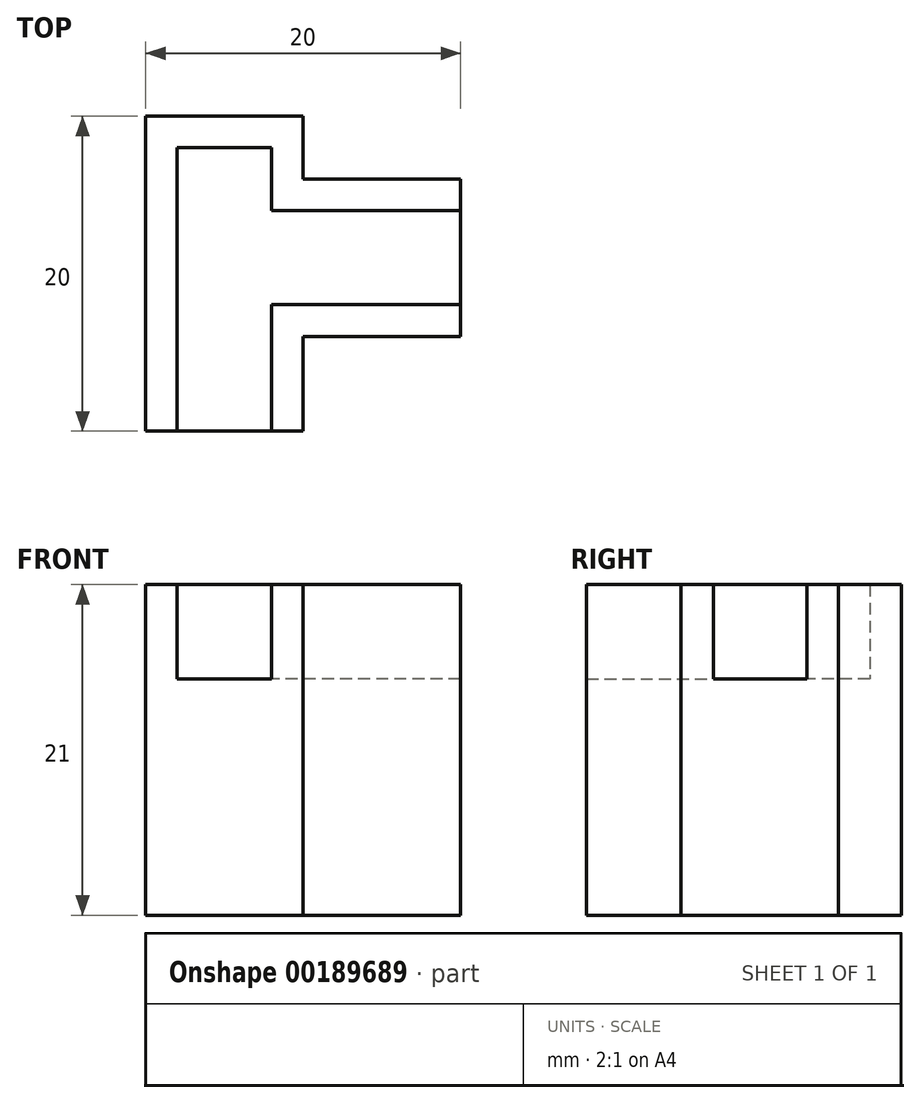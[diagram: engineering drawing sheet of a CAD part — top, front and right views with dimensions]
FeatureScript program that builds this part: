
annotation { "Feature Type Name" : "Feature", "Feature Type Description" : "" }
export const myFeature = defineFeature(function(context is Context, id is Id, definition is map)
    precondition{}
    {
        {
            var Q0;
            Q0=qCreatedBy(makeId("Top.planeOp"),FACE);
            var sketch = newSketch(context, id + "F0", { "sketchPlane" : qUnion([Q0])});
            skLineSegment(sketch, "E0.bottom", {"start": v(-93.24, 33.93) * mm, "end": v(-85.24, 33.93) * mm});
            skLineSegment(sketch, "E0.top", {"start": v(-83.24, 19.93) * mm, "end": v(-73.24, 19.93) * mm});
            skLineSegment(sketch, "E0.left", {"start": v(-93.24, 33.93) * mm, "end": v(-93.24, 19.93) * mm});
            skLineSegment(sketch, "E0.right", {"start": v(-73.24, 29.93) * mm, "end": v(-73.24, 19.93) * mm});
            skLineSegment(sketch, "E1.top", {"start": v(-93.24, 13.93) * mm, "end": v(-83.24, 13.93) * mm});
            skLineSegment(sketch, "E1.left", {"start": v(-93.24, 19.93) * mm, "end": v(-93.24, 13.93) * mm});
            skLineSegment(sketch, "E1.right", {"start": v(-83.24, 19.93) * mm, "end": v(-83.24, 13.93) * mm});
            skLineSegment(sketch, "E2.bottom", {"start": v(-85.24, 33.93) * mm, "end": v(-83.24, 33.93) * mm});
            skLineSegment(sketch, "E3.bottom", {"start": v(-93.24, 33.93) * mm, "end": v(-83.24, 33.93) * mm});
            skLineSegment(sketch, "E3.right", {"start": v(-83.24, 33.93) * mm, "end": v(-83.24, 29.93) * mm});
            skLineSegment(sketch, "E4.top", {"start": v(-73.24, 29.93) * mm, "end": v(-83.24, 29.93) * mm});
            skSolve(sketch);
        }
        {
            var Q0;
            Q0 = qSketchRegion(id + "F0", true);
            extrude(context, id + "F1", {"entities" : qUnion([Q0]), "depth" : 15 * mm});
        }
        {
            var Q0;
            Q0=makeQuery(id+"F1.opExtrude","CAP_FACE",FACE,{"disambiguationData":[OSD([sQuery(id+"F0.wireOp",EDGE,"E0.top"),sQuery(id+"F0.wireOp",EDGE,"E0.right"),sQuery(id+"F0.wireOp",EDGE,"E1.top"),sQuery(id+"F0.wireOp",EDGE,"E1.left"),sQuery(id+"F0.wireOp",EDGE,"E1.right"),sQuery(id+"F0.wireOp",EDGE,"E3.bottom"),sQuery(id+"F0.wireOp",EDGE,"E0.left"),sQuery(id+"F0.wireOp",EDGE,"E4.top"),sQuery(id+"F0.wireOp",EDGE,"E3.right")])],"isStart":false});
            var sketch = newSketch(context, id + "F2", { "sketchPlane" : qUnion([Q0])});
            skLineSegment(sketch, "E5.bottom", {"start": v(-93.24, 33.93) * mm, "end": v(-91.24, 33.93) * mm});
            skLineSegment(sketch, "E5.top", {"start": v(-93.24, 13.93) * mm, "end": v(-91.24, 13.93) * mm});
            skLineSegment(sketch, "E5.left", {"start": v(-93.24, 33.93) * mm, "end": v(-93.24, 13.93) * mm});
            skLineSegment(sketch, "E5.right", {"start": v(-91.24, 31.93) * mm, "end": v(-91.24, 13.93) * mm});
            skLineSegment(sketch, "E6.bottom", {"start": v(-83.24, 33.93) * mm, "end": v(-85.24, 33.93) * mm});
            skLineSegment(sketch, "E6.top", {"start": v(-83.24, 13.93) * mm, "end": v(-85.24, 13.93) * mm});
            skLineSegment(sketch, "E6.left", {"start": v(-83.24, 33.93) * mm, "end": v(-83.24, 29.93) * mm});
            skLineSegment(sketch, "E6.right", {"start": v(-85.24, 31.93) * mm, "end": v(-85.24, 27.93) * mm});
            skLineSegment(sketch, "E7.bottom", {"start": v(-93.24, 33.93) * mm, "end": v(-83.24, 33.93) * mm});
            skLineSegment(sketch, "E7.top", {"start": v(-91.24, 31.93) * mm, "end": v(-85.24, 31.93) * mm});
            skLineSegment(sketch, "E7.left", {"start": v(-93.24, 33.93) * mm, "end": v(-93.24, 31.93) * mm});
            skLineSegment(sketch, "E7.right", {"start": v(-83.24, 33.93) * mm, "end": v(-83.24, 31.93) * mm});
            skLineSegment(sketch, "E8.bottom", {"start": v(-83.24, 29.93) * mm, "end": v(-73.24, 29.93) * mm});
            skLineSegment(sketch, "E8.top", {"start": v(-85.24, 27.93) * mm, "end": v(-73.24, 27.93) * mm});
            skLineSegment(sketch, "E8.left", {"start": v(-85.24, 29.93) * mm, "end": v(-85.24, 27.93) * mm});
            skLineSegment(sketch, "E8.right", {"start": v(-73.24, 29.93) * mm, "end": v(-73.24, 27.93) * mm});
            skLineSegment(sketch, "E9.bottom", {"start": v(-73.24, 19.93) * mm, "end": v(-83.24, 19.93) * mm});
            skLineSegment(sketch, "E9.top", {"start": v(-73.24, 21.98) * mm, "end": v(-85.24, 21.98) * mm});
            skLineSegment(sketch, "E9.left", {"start": v(-73.24, 19.93) * mm, "end": v(-73.24, 21.98) * mm});
            skLineSegment(sketch, "E9.right", {"start": v(-85.24, 19.93) * mm, "end": v(-85.24, 21.98) * mm});
            skLineSegment(sketch, "E10.trimOffspring", {"start": v(-83.24, 19.93) * mm, "end": v(-83.24, 13.93) * mm});
            skLineSegment(sketch, "E11.trimOffspring", {"start": v(-85.24, 21.98) * mm, "end": v(-85.24, 13.93) * mm});
            skSolve(sketch);
        }
        {
            var Q0;
            {var subQ1=sQuery(id+"F2.wireOp",EDGE,"E6.top");Q0=makeQuery(id+"F2.imprint","IMPRINT",FACE,{"disambiguationData":[TD([[makeQuery(id+"F2.imprint","IMPRINT",EDGE,{"derivedFrom":subQ1}),1.0]])]});}
            var Q1;
            Q1=makeQuery(id+"F2.imprint","IMPRINT",FACE,{"disambiguationData":[TD([[makeQuery(id+"F2.imprint","IMPRINT",EDGE,{"derivedFrom":sQuery(id+"F2.wireOp",EDGE,"E5.top")}),1.0]])]});
            extrude(context, id + "F3", {"entities" : qUnion([Q0, Q1]), "operationType" : NewBodyOperationType.ADD, "depth" : 6 * mm});
        }
    });
